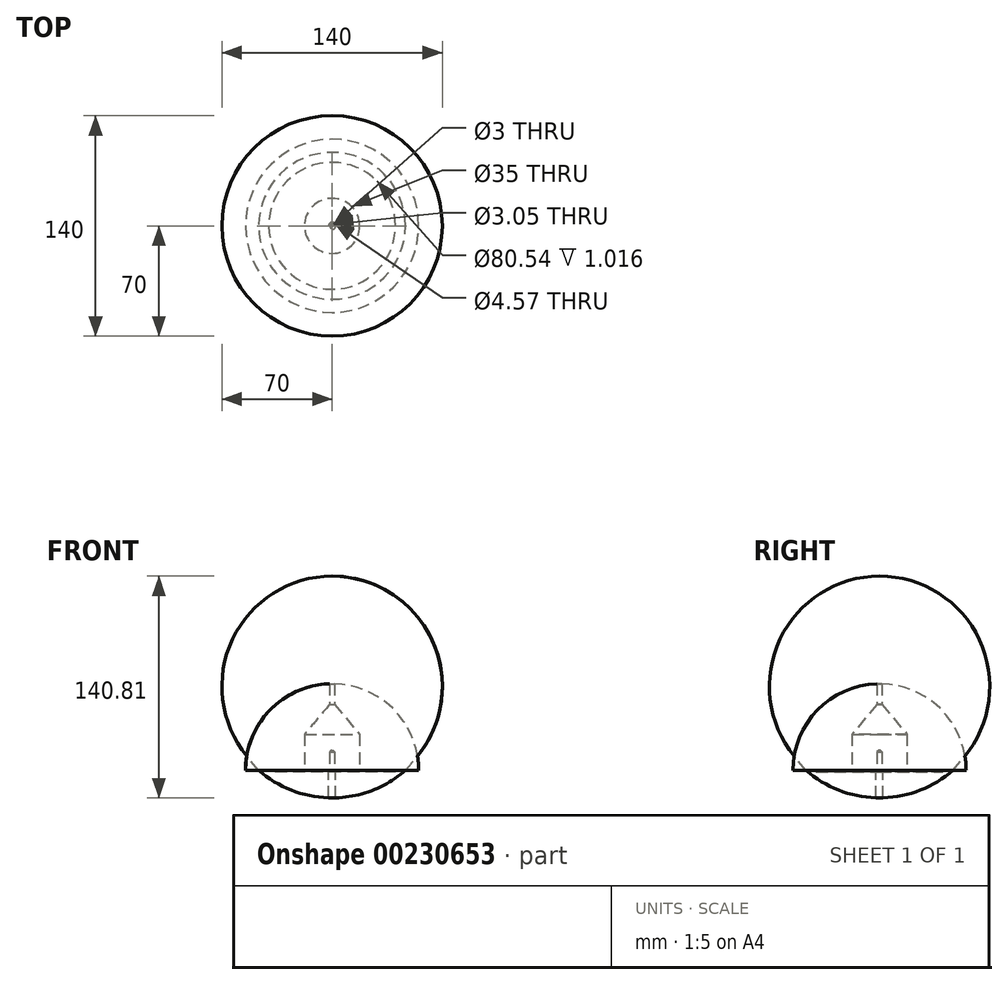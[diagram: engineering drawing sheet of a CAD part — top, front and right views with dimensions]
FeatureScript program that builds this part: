
annotation { "Feature Type Name" : "Feature", "Feature Type Description" : "" }
export const myFeature = defineFeature(function(context is Context, id is Id, definition is map)
    precondition{}
    {
        {
            var Q0;
            Q0=qCreatedBy(makeId("Front.planeOp"),FACE);
            var sketch = newSketch(context, id + "F0", { "sketchPlane" : qUnion([Q0])});
            skArc(sketch, "E0", {"start": v(53.62, 8.34) * mm, "mid": v(63.44, 82.92) * mm, "end": v(0, 123.34) * mm});
            skArc(sketch, "E1", {"start": v(47.44, 7.4) * mm, "mid": v(65.42, 62.4) * mm, "end": v(33.16, 110.45) * mm});
            skArc(sketch, "E2", {"start": v(33.16, 110.45) * mm, "mid": v(5.25, 61.13) * mm, "end": v(23.26, 7.4) * mm});
            skLineSegment(sketch, "E3", {"start": v(0, 123.34) * mm, "end": v(0, 0) * mm});
            skLineSegment(sketch, "E4", {"start": v(0, 0) * mm, "end": v(46.62, 0) * mm});
            skLineSegment(sketch, "E5", {"start": v(0, 0) * mm, "end": v(0, -57.5) * mm, "construction": true});
            skLineSegment(sketch, "E6", {"start": v(47.44, 7.4) * mm, "end": v(23.26, 7.4) * mm});
            skLineSegment(sketch, "E7", {"start": v(53.62, 8.34) * mm, "end": v(46.62, 0) * mm});
            skSolve(sketch);
        }
        {
            var Q0;
            Q0=makeQuery(id+"F0.imprint","IMPRINT",FACE,{"disambiguationData":[TD([[makeQuery(id+"F0.imprint","IMPRINT",EDGE,{"derivedFrom":sQuery(id+"F0.wireOp",EDGE,"E0")}),1.0]])]});
            var Q1;
            Q1=makeQuery(id+"F0.imprint","IMPRINT",FACE,{"disambiguationData":[TD([[makeQuery(id+"F0.imprint","IMPRINT",EDGE,{"derivedFrom":sQuery(id+"F0.wireOp",EDGE,"E1")}),1.0]])]});
            var Q2;
            Q2=sQuery(id+"F0.wireOp",EDGE,"E5");
            revolve(context, id + "F1", {"entities" : qUnion([Q0, Q1]), "axis" : qUnion([Q2]), "revolveType" : RevolveType.FULL});
        }
        {
            var Q0;
            Q0=makeQuery(id+"F1.opRevolve","SWEPT_FACE",FACE,{"disambiguationData":[OSD([sQuery(id+"F0.wireOp",EDGE,"E4")])]});
            var sketch = newSketch(context, id + "F2", { "sketchPlane" : qUnion([Q0])});
            skCircle(sketch, "E8", {"center": v(0, 0) * mm, "radius": 1.52 * mm});
            skSolve(sketch);
        }
        {
            var Q0;
            Q0=qSketchRegion(id+"F2",true);
            extrude(context, id + "F3", {"entities" : qUnion([Q0]), "operationType" : NewBodyOperationType.REMOVE, "oppositeDirection" : true, "depth" : 12.7 * mm});
        }
        {
            var Q0;
            Q0=makeQuery(id+"F3.boolean.opBoolean","COPY",EDGE,{"derivedFrom":makeQuery(id+"F3.opExtrude","CAP_EDGE",EDGE,{"disambiguationData":[OSD([sQuery(id+"F2.wireOp",EDGE,"E8")])],"isStart":false})});
            chamfer(context, id + "F4", {"entities" : qUnion([Q0]), "width" : 1.02 * mm, "tangentPropagation" : true});
        }
        {
            var Q0;
            Q0=qCreatedBy(makeId("Front.planeOp"),FACE);
            var sketch = newSketch(context, id + "F5", { "sketchPlane" : qUnion([Q0])});
            skArc(sketch, "E9", {"start": v(0, -17.5) * mm, "mid": v(24.9, -12.98) * mm, "end": v(46.62, 0) * mm});
            skLineSegment(sketch, "E10", {"start": v(46.62, 0) * mm, "end": v(40.27, 0) * mm});
            skLineSegment(sketch, "E11", {"start": v(40.27, 0) * mm, "end": v(40.27, -1.02) * mm});
            skLineSegment(sketch, "E12", {"start": v(40.27, -1.02) * mm, "end": v(0, -1.02) * mm});
            skLineSegment(sketch, "E13", {"start": v(0, -1.02) * mm, "end": v(0, -17.5) * mm});
            skSolve(sketch);
        }
        {
            var Q0;
            Q0=qSketchRegion(id+"F5",true);
            var Q1;
            Q1=sQuery(id+"F0.wireOp",EDGE,"E5");
            revolve(context, id + "F6", {"entities" : qUnion([Q0]), "axis" : qUnion([Q1]), "revolveType" : RevolveType.FULL});
        }
        {
            var Q0;
            Q0=makeQuery(id+"F6.opRevolve","SWEPT_FACE",FACE,{"disambiguationData":[OSD([sQuery(id+"F5.wireOp",EDGE,"E12")])]});
            var sketch = newSketch(context, id + "F7", { "sketchPlane" : qUnion([Q0])});
            skCircle(sketch, "E14", {"center": v(0, 0) * mm, "radius": 2.29 * mm});
            skSolve(sketch);
        }
        {
            var Q0;
            Q0=qSketchRegion(id+"F7",true);
            extrude(context, id + "F8", {"entities" : qUnion([Q0]), "operationType" : NewBodyOperationType.REMOVE, "oppositeDirection" : true, "depth" : 25.4 * mm});
        }
        {
            var Q0;
            Q0=qCreatedBy(makeId("Front.planeOp"),FACE);
            var sketch = newSketch(context, id + "F9", { "sketchPlane" : qUnion([Q0])});
            skArc(sketch, "E15", {"start": v(55, 0) * mm, "mid": v(39.42, 38.36) * mm, "end": v(1.5, 54.98) * mm});
            skLineSegment(sketch, "E16", {"start": v(17.5, 0) * mm, "end": v(55, 0) * mm});
            skLineSegment(sketch, "E17", {"start": v(0, 0) * mm, "end": v(0, 55) * mm, "construction": true});
            skLineSegment(sketch, "E18", {"start": v(1.5, 54.98) * mm, "end": v(1.5, 41.98) * mm});
            skLineSegment(sketch, "E19", {"start": v(1.5, 41.98) * mm, "end": v(17.5, 22.91) * mm});
            skLineSegment(sketch, "E20", {"start": v(17.5, 22.91) * mm, "end": v(17.5, 0) * mm});
            skSolve(sketch);
        }
        {
            var Q0;
            Q0 = qSketchRegion(id + "F9", true);
            var Q1;
            Q1=sQuery(id+"F9.wireOp",EDGE,"E17");
            revolve(context, id + "F10", {"entities" : qUnion([Q0]), "axis" : qUnion([Q1]), "revolveType" : RevolveType.FULL});
        }
    });
